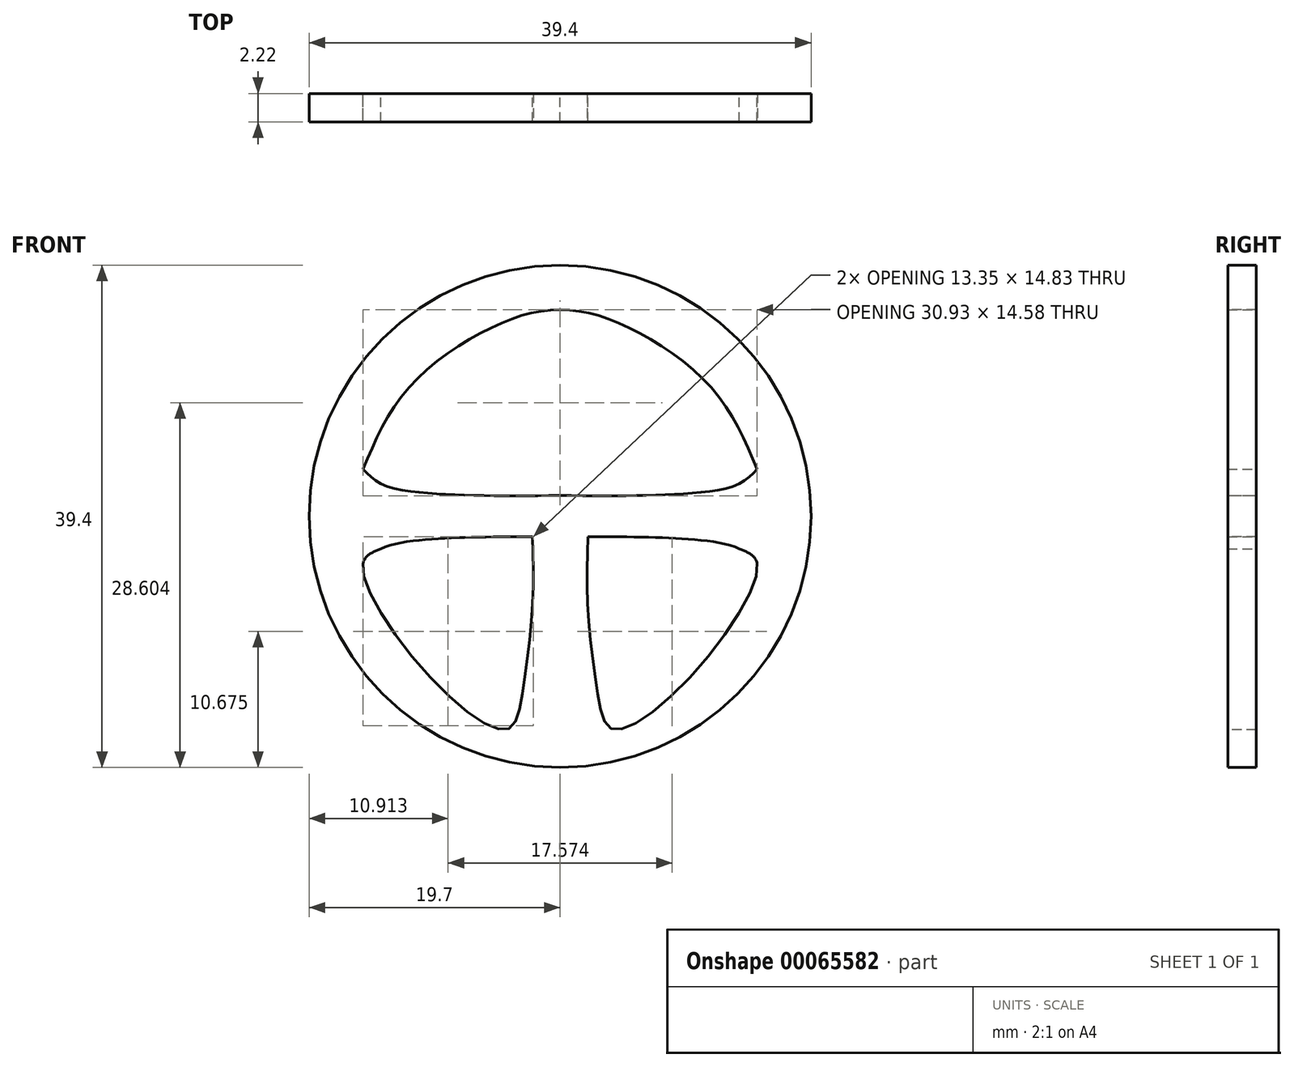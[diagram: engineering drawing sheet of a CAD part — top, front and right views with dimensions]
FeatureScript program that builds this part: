
annotation { "Feature Type Name" : "Feature", "Feature Type Description" : "" }
export const myFeature = defineFeature(function(context is Context, id is Id, definition is map)
    precondition{}
    {
        {
            var Q0;
            Q0=qCreatedBy(makeId("Front.planeOp"),FACE);
            var sketch = newSketch(context, id + "F0", { "sketchPlane" : qUnion([Q0])});
            skCircle(sketch, "E0", {"center": v(0, 0) * mm, "radius": 19.7 * mm});
            skSolve(sketch);
        }
        {
            var Q0;
            Q0=qCreatedBy(makeId("Front.planeOp"),FACE);
            var sketch = newSketch(context, id + "F1", { "sketchPlane" : qUnion([Q0])});
            skFitSpline(sketch, "E1", {"points": [v(-15.46, 3.71) * mm, v(-14.08, 2.55) * mm, v(-10.84, 1.86) * mm, v(-6.3, 1.63) * mm, v(0, 1.63) * mm], "startDerivative": vector(6.84, -7.46) * mm, "endDerivative": vector(20.34, 0.16) * mm});
            skFitSpline(sketch, "E2.MirrorCS", {"points": [v(15.46, 3.71) * mm, v(14.08, 2.55) * mm, v(10.84, 1.86) * mm, v(6.3, 1.63) * mm, v(0, 1.63) * mm], "startDerivative": vector(-6.84, -7.46) * mm, "endDerivative": vector(-20.34, 0.16) * mm});
            skFitSpline(sketch, "E3.MirrorCS", {"points": [v(-15.46, -3.71) * mm, v(-14.08, -2.55) * mm, v(-10.84, -1.86) * mm, v(-6.3, -1.63) * mm, v(0, -1.63) * mm], "startDerivative": vector(6.84, 7.46) * mm, "endDerivative": vector(20.34, -0.16) * mm});
            skFitSpline(sketch, "E4", {"points": [v(-2.18, -1.61) * mm, v(-2.18, -7.31) * mm, v(-2.98, -14.01) * mm, v(-4.13, -16.71) * mm, v(-10.68, -12.09) * mm, v(-15.46, -3.71) * mm, v(-14.08, -2.55) * mm], "startDerivative": vector(1.08, -32.16) * mm, "endDerivative": vector(19.6, 7.66) * mm});
            skFitSpline(sketch, "E5.MirrorCS", {"points": [v(2.18, -1.61) * mm, v(2.18, -7.31) * mm, v(2.98, -14.01) * mm, v(4.13, -16.71) * mm, v(10.68, -12.09) * mm, v(15.46, -3.71) * mm, v(14.08, -2.55) * mm], "startDerivative": vector(-1.08, -32.16) * mm, "endDerivative": vector(-19.6, 7.66) * mm});
            skFitSpline(sketch, "E6.MirrorCS", {"points": [v(15.46, -3.71) * mm, v(14.08, -2.55) * mm, v(10.84, -1.86) * mm, v(6.3, -1.63) * mm, v(0, -1.63) * mm], "startDerivative": vector(-6.84, 7.46) * mm, "endDerivative": vector(-20.34, -0.16) * mm});
            skFitSpline(sketch, "E7", {"points": [v(-15.46, 3.71) * mm, v(-12, 9.95) * mm, v(-5.21, 14.89) * mm, v(0, 16.2) * mm], "startDerivative": vector(8.04, 18.83) * mm, "endDerivative": vector(17.25, -0.26) * mm});
            skFitSpline(sketch, "E8.MirrorCS", {"points": [v(15.46, 3.71) * mm, v(12, 9.95) * mm, v(5.21, 14.89) * mm, v(0, 16.2) * mm], "startDerivative": vector(-8.04, 18.83) * mm, "endDerivative": vector(-17.25, -0.26) * mm});
            skSolve(sketch);
        }
        {
            var Q0;
            Q0 = qSketchRegion(id + "F0", true);
            extrude(context, id + "F2", {"entities" : qUnion([Q0]), "depth" : 2.22 * mm});
        }
        {
            var Q0;
            Q0 = qSketchRegion(id + "F1", true);
            extrude(context, id + "F3", {"entities" : qUnion([Q0]), "operationType" : NewBodyOperationType.REMOVE, "depth" : 50.8 * mm});
        }
    });
